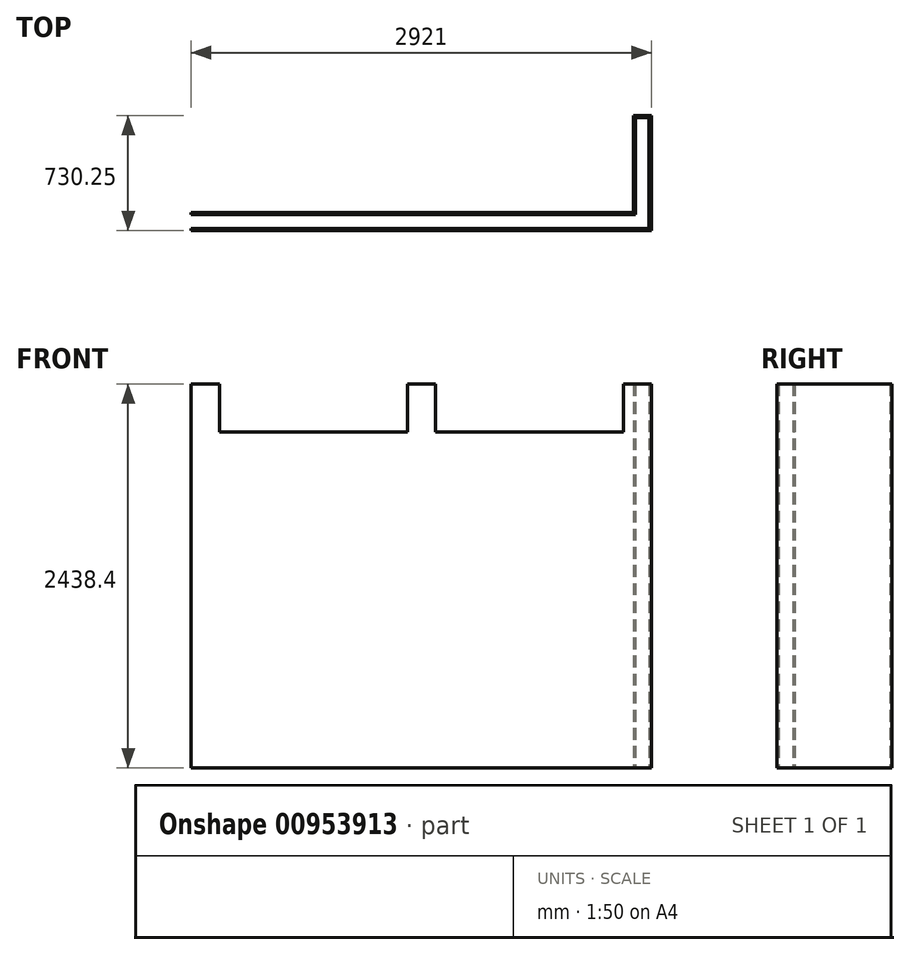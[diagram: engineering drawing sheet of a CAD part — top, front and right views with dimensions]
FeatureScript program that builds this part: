
annotation { "Feature Type Name" : "Feature", "Feature Type Description" : "" }
export const myFeature = defineFeature(function(context is Context, id is Id, definition is map)
    precondition{}
    {
        {
            var Q0;
            Q0=qCreatedBy(makeId("Top.planeOp"),FACE);
            var sketch = newSketch(context, id + "F0", { "sketchPlane" : qUnion([Q0])});
            skLineSegment(sketch, "E0", {"start": v(0, 0) * mm, "end": v(2921, 0) * mm});
            skLineSegment(sketch, "E1", {"start": v(2921, 0) * mm, "end": v(2921, 730.25) * mm});
            skLineSegment(sketch, "E2", {"start": v(2921, 730.25) * mm, "end": v(2806.7, 730.25) * mm});
            skLineSegment(sketch, "E3", {"start": v(2806.7, 730.25) * mm, "end": v(2806.7, 114.3) * mm});
            skLineSegment(sketch, "E4", {"start": v(2806.7, 114.3) * mm, "end": v(0, 114.3) * mm});
            skLineSegment(sketch, "E5", {"start": v(0, 114.3) * mm, "end": v(0, 0) * mm});
            skSolve(sketch);
        }
        {
            var Q0;
            Q0 = qSketchRegion(id + "F0", true);
            extrude(context, id + "F1", {"entities" : qUnion([Q0]), "depth" : 2438.4 * mm, "offsetDistance" : 25.4 * mm});
        }
        {
            var Q0;
            Q0=makeQuery(id+"F1.opExtrude","SWEPT_FACE",FACE,{"disambiguationData":[OSD([sQuery(id+"F0.wireOp",EDGE,"E0")])]});
            var sketch = newSketch(context, id + "F2", { "sketchPlane" : qUnion([Q0])});
            skLineSegment(sketch, "E6.bottom", {"start": v(177.8, 2438.4) * mm, "end": v(1371.6, 2438.4) * mm});
            skLineSegment(sketch, "E6.top", {"start": v(177.8, 2133.6) * mm, "end": v(1371.6, 2133.6) * mm});
            skLineSegment(sketch, "E6.left", {"start": v(177.8, 2438.4) * mm, "end": v(177.8, 2133.6) * mm});
            skLineSegment(sketch, "E6.right", {"start": v(1371.6, 2438.4) * mm, "end": v(1371.6, 2133.6) * mm});
            skLineSegment(sketch, "E7.bottom", {"start": v(1549.4, 2438.4) * mm, "end": v(2743.2, 2438.4) * mm});
            skLineSegment(sketch, "E7.top", {"start": v(1549.4, 2133.6) * mm, "end": v(2743.2, 2133.6) * mm});
            skLineSegment(sketch, "E7.left", {"start": v(1549.4, 2438.4) * mm, "end": v(1549.4, 2133.6) * mm});
            skLineSegment(sketch, "E7.right", {"start": v(2743.2, 2438.4) * mm, "end": v(2743.2, 2133.6) * mm});
            skSolve(sketch);
        }
        {
            var Q0;
            Q0 = qSketchRegion(id + "F2", true);
            extrude(context, id + "F3", {"entities" : qUnion([Q0]), "operationType" : NewBodyOperationType.REMOVE, "endBound" : BoundingType.THROUGH_ALL, "oppositeDirection" : true, "depth" : 25.4 * mm, "offsetDistance" : 25.4 * mm});
        }
        {
            var Q0;
            Q0=makeQuery(id+"F1.opExtrude","SWEPT_FACE",FACE,{"disambiguationData":[OSD([sQuery(id+"F0.wireOp",EDGE,"E0")])]});
            var sketch = newSketch(context, id + "F4", { "sketchPlane" : qUnion([Q0])});
            skLineSegment(sketch, "E8.bottom", {"start": v(177.8, 2438.4) * mm, "end": v(2743.2, 2438.4) * mm});
            skLineSegment(sketch, "E8.top", {"start": v(177.8, 2400.3) * mm, "end": v(2743.2, 2400.3) * mm});
            skLineSegment(sketch, "E8.left", {"start": v(177.8, 2438.4) * mm, "end": v(177.8, 2400.3) * mm});
            skLineSegment(sketch, "E8.right", {"start": v(2743.2, 2438.4) * mm, "end": v(2743.2, 2400.3) * mm});
            skSolve(sketch);
        }
        {
            var Q0;
            {var subQ0=sQuery(id+"F0.wireOp",EDGE,"E0");var subQ1=sQuery(id+"F0.wireOp",EDGE,"E4");var subQ2=sQuery(id+"F0.wireOp",EDGE,"E5");Q0=makeQuery(id+"F3.boolean.opBoolean","SPLIT",FACE,{"disambiguationData":[TD([makeQuery(id+"F1.opExtrude","SWEPT_FACE",FACE,{"disambiguationData":[OSD([subQ2])]})])],"derivedFrom":makeQuery(id+"F1.opExtrude","CAP_FACE",FACE,{"disambiguationData":[OSD([subQ0,sQuery(id+"F0.wireOp",EDGE,"E1"),sQuery(id+"F0.wireOp",EDGE,"E2"),sQuery(id+"F0.wireOp",EDGE,"E3"),subQ1,subQ2])],"isStart":false})});}
            var Q1;
            {var subQ0=sQuery(id+"F0.wireOp",EDGE,"E0");var subQ1=sQuery(id+"F0.wireOp",EDGE,"E4");Q1=makeQuery(id+"F3.boolean.opBoolean","SPLIT",FACE,{"disambiguationData":[TD([makeQuery(id+"F3.opExtrude","SWEPT_FACE",FACE,{"disambiguationData":[OSD([sQuery(id+"F2.wireOp",EDGE,"E6.right")])]})])],"derivedFrom":makeQuery(id+"F1.opExtrude","CAP_FACE",FACE,{"disambiguationData":[OSD([subQ0,sQuery(id+"F0.wireOp",EDGE,"E1"),sQuery(id+"F0.wireOp",EDGE,"E2"),sQuery(id+"F0.wireOp",EDGE,"E3"),subQ1,sQuery(id+"F0.wireOp",EDGE,"E5")])],"isStart":false})});}
            var Q2;
            {var subQ0=sQuery(id+"F0.wireOp",EDGE,"E2");var subQ1=sQuery(id+"F0.wireOp",EDGE,"E1");var subQ2=sQuery(id+"F0.wireOp",EDGE,"E3");var subQ3=sQuery(id+"F0.wireOp",EDGE,"E0");var subQ4=sQuery(id+"F0.wireOp",EDGE,"E4");Q2=makeQuery(id+"F3.boolean.opBoolean","SPLIT",FACE,{"disambiguationData":[TD([makeQuery(id+"F1.opExtrude","SWEPT_FACE",FACE,{"disambiguationData":[OSD([subQ1])]})])],"derivedFrom":makeQuery(id+"F1.opExtrude","CAP_FACE",FACE,{"disambiguationData":[OSD([subQ3,subQ1,subQ0,subQ2,subQ4,sQuery(id+"F0.wireOp",EDGE,"E5")])],"isStart":false})});}
            var Q3;
            Q3=makeQuery(id+"F1.opExtrude","SWEPT_FACE",FACE,{"disambiguationData":[OSD([sQuery(id+"F0.wireOp",EDGE,"E5")])]});
            var Q4;
            Q4=makeQuery(id+"F1.opExtrude","CAP_FACE",FACE,{"disambiguationData":[OSD([sQuery(id+"F0.wireOp",EDGE,"E0"),sQuery(id+"F0.wireOp",EDGE,"E1"),sQuery(id+"F0.wireOp",EDGE,"E2"),sQuery(id+"F0.wireOp",EDGE,"E3"),sQuery(id+"F0.wireOp",EDGE,"E4"),sQuery(id+"F0.wireOp",EDGE,"E5")])],"isStart":true});
            var Q5;
            Q5=makeQuery(id+"F3.boolean.opBoolean","COPY",FACE,{"derivedFrom":makeQuery(id+"F3.opExtrude","SWEPT_FACE",FACE,{"disambiguationData":[OSD([sQuery(id+"F2.wireOp",EDGE,"E6.left")])]})});
            var Q6;
            Q6=makeQuery(id+"F3.boolean.opBoolean","COPY",FACE,{"derivedFrom":makeQuery(id+"F3.opExtrude","SWEPT_FACE",FACE,{"disambiguationData":[OSD([sQuery(id+"F2.wireOp",EDGE,"E6.top")])]})});
            var Q7;
            Q7=makeQuery(id+"F3.boolean.opBoolean","COPY",FACE,{"derivedFrom":makeQuery(id+"F3.opExtrude","SWEPT_FACE",FACE,{"disambiguationData":[OSD([sQuery(id+"F2.wireOp",EDGE,"E7.left")])]})});
            var Q8;
            Q8=makeQuery(id+"F3.boolean.opBoolean","COPY",FACE,{"derivedFrom":makeQuery(id+"F3.opExtrude","SWEPT_FACE",FACE,{"disambiguationData":[OSD([sQuery(id+"F2.wireOp",EDGE,"E7.top")])]})});
            var Q9;
            Q9=makeQuery(id+"F3.boolean.opBoolean","COPY",FACE,{"derivedFrom":makeQuery(id+"F3.opExtrude","SWEPT_FACE",FACE,{"disambiguationData":[OSD([sQuery(id+"F2.wireOp",EDGE,"E6.right")])]})});
            var Q10;
            Q10=makeQuery(id+"F3.boolean.opBoolean","COPY",FACE,{"derivedFrom":makeQuery(id+"F3.opExtrude","SWEPT_FACE",FACE,{"disambiguationData":[OSD([sQuery(id+"F2.wireOp",EDGE,"E7.right")])]})});
            shell(context, id + "F5", {"entities" : qUnion([Q0, Q1, Q2, Q3, Q4, Q5, Q6, Q7, Q8, Q9, Q10]), "thickness" : 12.7 * mm});
        }
    });
